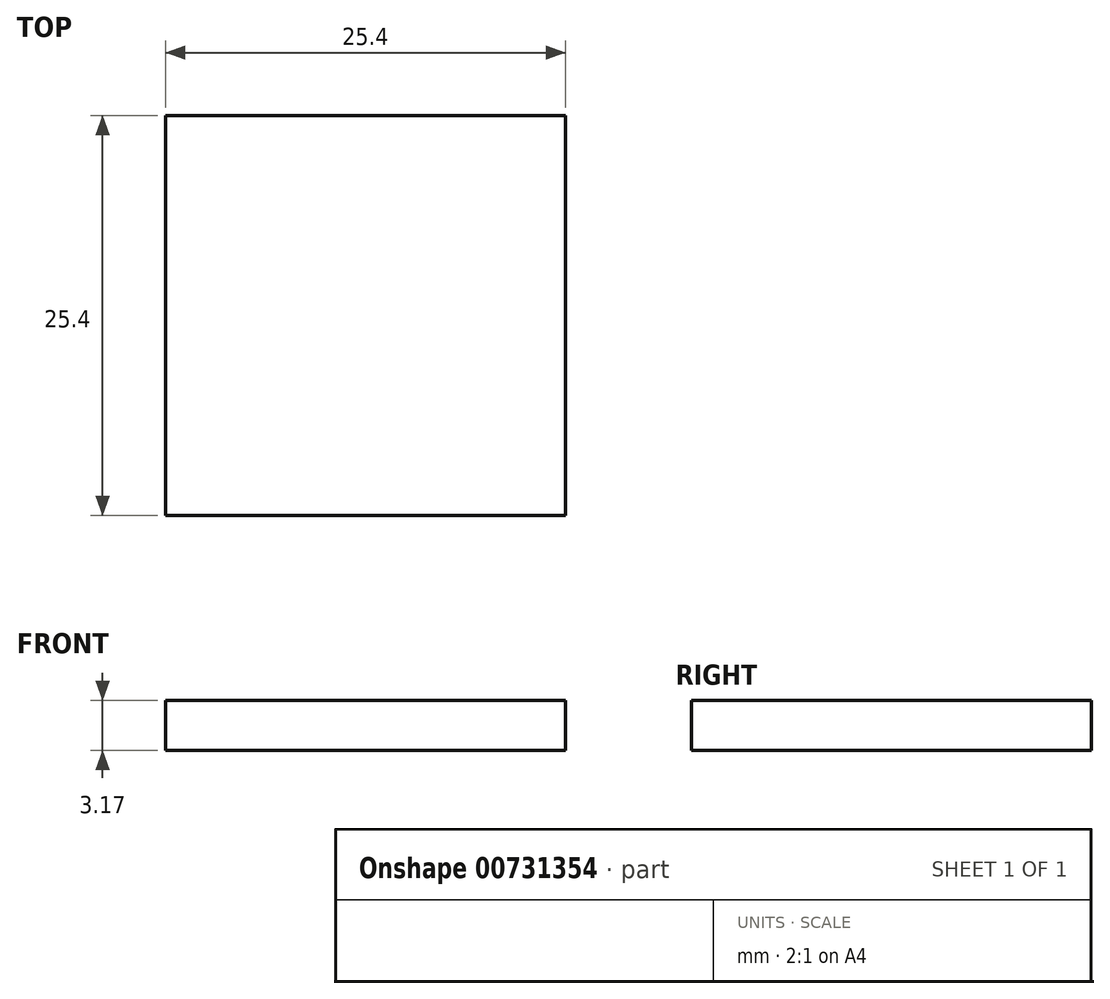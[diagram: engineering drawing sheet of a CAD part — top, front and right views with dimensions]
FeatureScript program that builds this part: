
annotation { "Feature Type Name" : "Feature", "Feature Type Description" : "" }
export const myFeature = defineFeature(function(context is Context, id is Id, definition is map)
    precondition{}
    {
        {
            var Q0;
            Q0=qCreatedBy(makeId("Top.planeOp"),FACE);
            var sketch = newSketch(context, id + "F0", { "sketchPlane" : qUnion([Q0])});
            skLineSegment(sketch, "E0.bottom", {"start": v(-12.7, 25.4) * mm, "end": v(12.7, 25.4) * mm});
            skLineSegment(sketch, "E0.top", {"start": v(-12.7, 0) * mm, "end": v(12.7, 0) * mm});
            skLineSegment(sketch, "E0.left", {"start": v(-12.7, 25.4) * mm, "end": v(-12.7, 0) * mm});
            skLineSegment(sketch, "E0.right", {"start": v(12.7, 25.4) * mm, "end": v(12.7, 0) * mm});
            skSolve(sketch);
        }
        {
            var Q0;
            Q0=makeQuery(id+"F0.imprint","IMPRINT",FACE,{"disambiguationData":[TD([[makeQuery(id+"F0.imprint","IMPRINT",EDGE,{"derivedFrom":sQuery(id+"F0.wireOp",EDGE,"E0.bottom")}),-1.0]])]});
            extrude(context, id + "F1", {"entities" : qUnion([Q0]), "depth" : 3.17 * mm, "offsetDistance" : 25.4 * mm});
        }
    });
